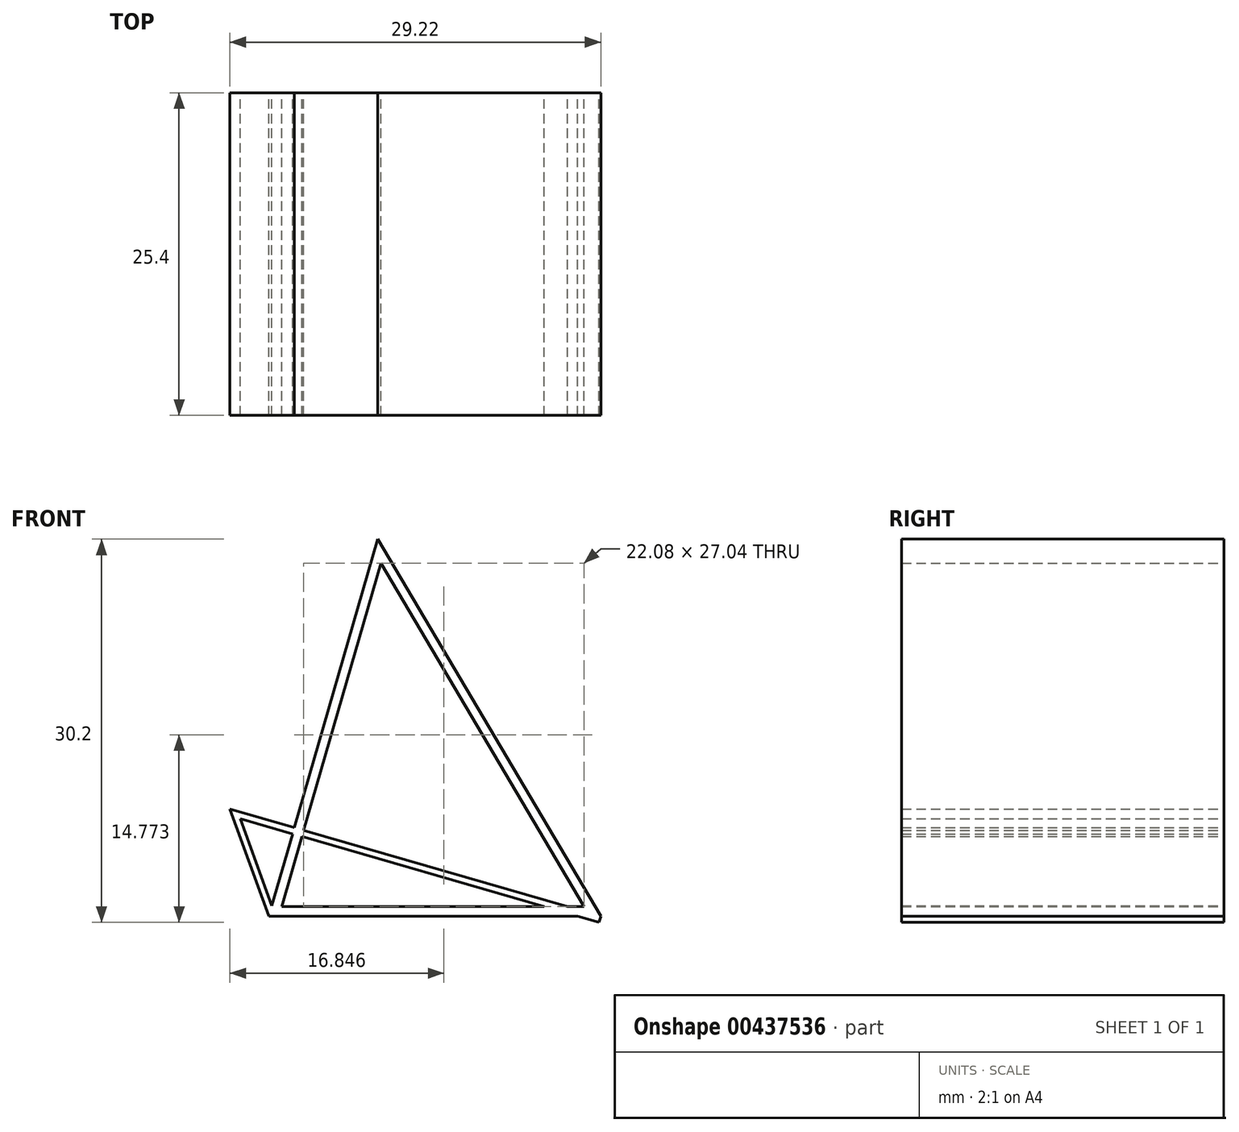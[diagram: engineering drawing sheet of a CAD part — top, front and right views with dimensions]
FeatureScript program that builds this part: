
annotation { "Feature Type Name" : "Feature", "Feature Type Description" : "" }
export const myFeature = defineFeature(function(context is Context, id is Id, definition is map)
    precondition{}
    {
        {
            var Q0;
            Q0=qCreatedBy(makeId("Front.planeOp"),FACE);
            var sketch = newSketch(context, id + "F0", { "sketchPlane" : qUnion([Q0])});
            skLineSegment(sketch, "E0", {"start": v(0, 0) * mm, "end": v(26.16, 0) * mm});
            skLineSegment(sketch, "E1", {"start": v(26.16, 0) * mm, "end": v(8.58, 29.71) * mm});
            skLineSegment(sketch, "E2", {"start": v(8.58, 29.71) * mm, "end": v(0, 0) * mm});
            skLineSegment(sketch, "E3", {"start": v(26.16, 0) * mm, "end": v(-3.06, 8.44) * mm});
            skLineSegment(sketch, "E4", {"start": v(-3.06, 8.44) * mm, "end": v(0, 0) * mm});
            skLineSegment(sketch, "E5.0", {"start": v(8.83, 27.8) * mm, "end": v(1.01, 0.76) * mm});
            skLineSegment(sketch, "E5.1", {"start": v(24.82, 0.76) * mm, "end": v(8.83, 27.8) * mm});
            skLineSegment(sketch, "E5.2", {"start": v(1.01, 0.76) * mm, "end": v(24.82, 0.76) * mm});
            skLineSegment(sketch, "E6.0", {"start": v(-2.24, 7.67) * mm, "end": v(0.48, 0.17) * mm});
            skLineSegment(sketch, "E6.1", {"start": v(26.02, -0.49) * mm, "end": v(-2.24, 7.67) * mm});
            skLineSegment(sketch, "E7", {"start": v(26.16, 0) * mm, "end": v(26.02, -0.49) * mm});
            skLineSegment(sketch, "E8", {"start": v(0.48, 0.17) * mm, "end": v(0, 0) * mm});
            skSolve(sketch);
        }
        {
            var Q0;
            {var subQ0=sQuery(id+"F0.wireOp",EDGE,"E7");Q0=makeQuery(id+"F0.imprint","IMPRINT",FACE,{"disambiguationData":[TD([[makeQuery(id+"F0.imprint","IMPRINT",EDGE,{"derivedFrom":subQ0}),-1.0]])]});}
            var Q1;
            {var subQ0=sQuery(id+"F0.wireOp",EDGE,"E8");Q1=makeQuery(id+"F0.imprint","IMPRINT",FACE,{"disambiguationData":[TD([[makeQuery(id+"F0.imprint","IMPRINT",EDGE,{"derivedFrom":subQ0}),-1.0]])]});}
            var Q2;
            {var subQ5=sQuery(id+"F0.wireOp",EDGE,"E1");Q2=makeQuery(id+"F0.imprint","IMPRINT",FACE,{"disambiguationData":[TD([[makeQuery(id+"F0.imprint","IMPRINT",EDGE,{"derivedFrom":subQ5}),1.0]])]});}
            var Q3;
            {var subQ0=sQuery(id+"F0.wireOp",EDGE,"E4");Q3=makeQuery(id+"F0.imprint","IMPRINT",FACE,{"disambiguationData":[TD([[makeQuery(id+"F0.imprint","IMPRINT",EDGE,{"derivedFrom":subQ0}),1.0]])]});}
            var Q4;
            {var subQ0=sQuery(id+"F0.wireOp",EDGE,"E3");var subQ5=sQuery(id+"F0.wireOp",EDGE,"E5.2");var subQ6=makeQuery(id+"F0.imprint","INTERSECT",VERTEX,{"derivedFrom":[subQ0,subQ5]});Q4=makeQuery(id+"F0.imprint","IMPRINT",FACE,{"disambiguationData":[TD([[makeQuery(id+"F0.imprint","IMPRINT",EDGE,{"disambiguationData":[TD([[subQ6,1.0]])],"derivedFrom":subQ5}),-1.0]])]});}
            var Q5;
            {var subQ0=sQuery(id+"F0.wireOp",EDGE,"E3");var subQ1=sQuery(id+"F0.wireOp",EDGE,"E2");var subQ2=makeQuery(id+"F0.imprint","INTERSECT",VERTEX,{"derivedFrom":[subQ1,subQ0]});Q5=makeQuery(id+"F0.imprint","IMPRINT",FACE,{"disambiguationData":[TD([[makeQuery(id+"F0.imprint","IMPRINT",EDGE,{"disambiguationData":[TD([[subQ2,-1.0]])],"derivedFrom":subQ1}),1.0]])]});}
            var Q6;
            {var subQ0=sQuery(id+"F0.wireOp",EDGE,"E5.2");var subQ1=sQuery(id+"F0.wireOp",EDGE,"E3");var subQ2=makeQuery(id+"F0.imprint","INTERSECT",VERTEX,{"derivedFrom":[subQ1,subQ0]});Q6=makeQuery(id+"F0.imprint","IMPRINT",FACE,{"disambiguationData":[TD([[makeQuery(id+"F0.imprint","IMPRINT",EDGE,{"disambiguationData":[TD([[subQ2,-1.0]])],"derivedFrom":subQ1}),1.0]])]});}
            var Q7;
            {var subQ9=sQuery(id+"F0.wireOp",EDGE,"E8");Q7=makeQuery(id+"F0.imprint","IMPRINT",FACE,{"disambiguationData":[TD([[makeQuery(id+"F0.imprint","IMPRINT",EDGE,{"derivedFrom":subQ9}),1.0]])]});}
            extrude(context, id + "F1", {"entities" : qUnion([Q0, Q1, Q2, Q3, Q4, Q5, Q6, Q7]), "depth" : 25.4 * mm});
        }
    });
